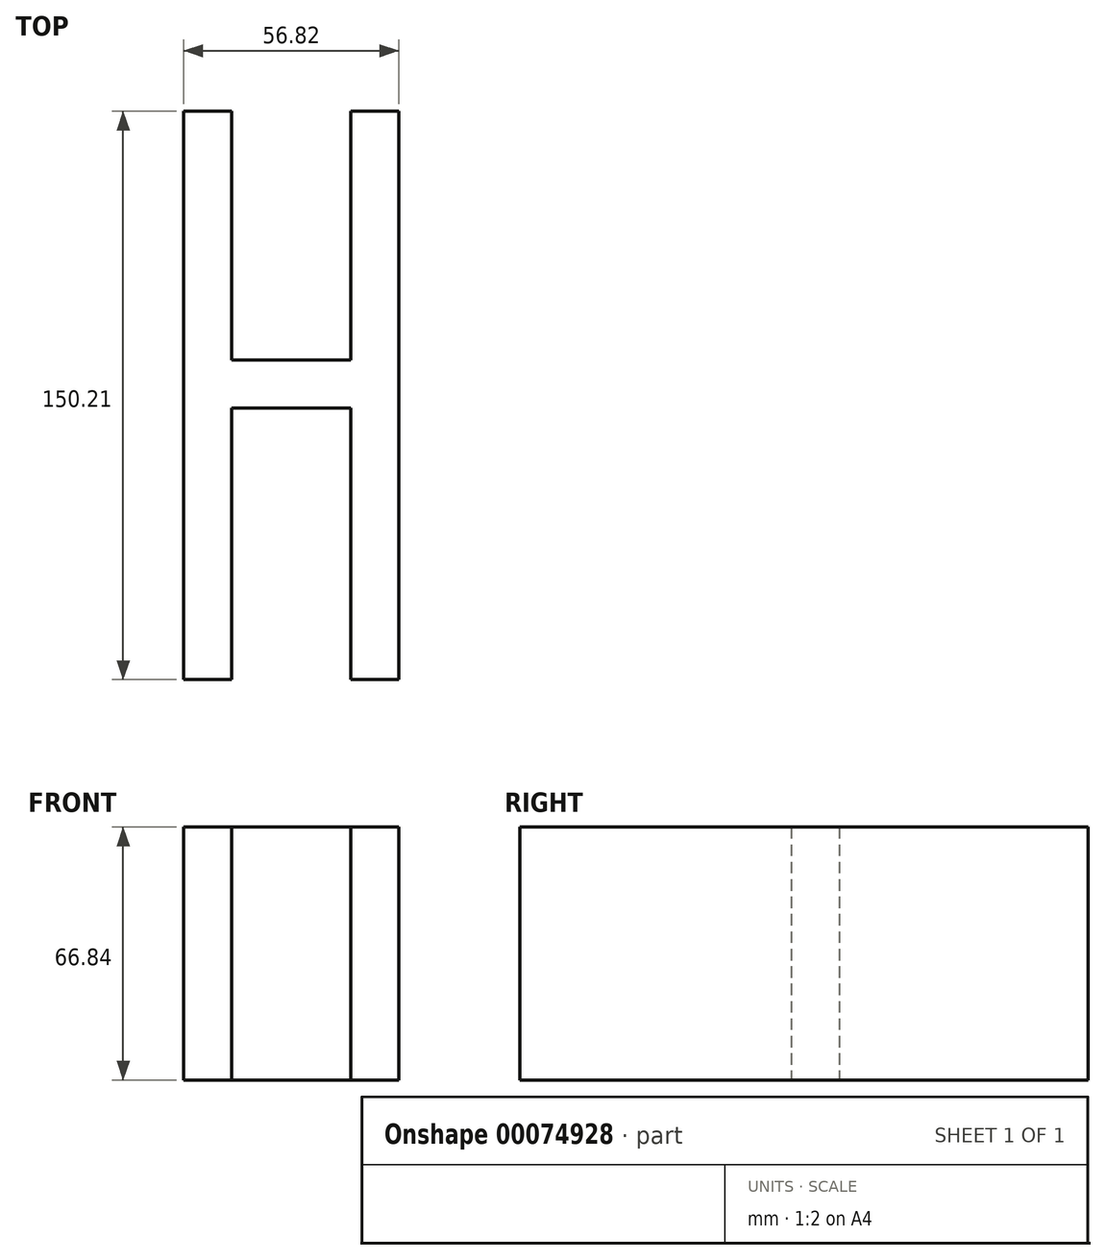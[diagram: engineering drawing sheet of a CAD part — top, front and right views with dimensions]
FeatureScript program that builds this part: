
annotation { "Feature Type Name" : "Feature", "Feature Type Description" : "" }
export const myFeature = defineFeature(function(context is Context, id is Id, definition is map)
    precondition{}
    {
        {
            var Q0;
            Q0=qCreatedBy(makeId("Top.planeOp"),FACE);
            var sketch = newSketch(context, id + "F0", { "sketchPlane" : qUnion([Q0])});
            skLineSegment(sketch, "E0.bottom", {"start": v(-111.8, 73) * mm, "end": v(-99.1, 73) * mm});
            skLineSegment(sketch, "E0.top", {"start": v(-111.8, -77.21) * mm, "end": v(-99.1, -77.21) * mm});
            skLineSegment(sketch, "E0.left", {"start": v(-111.8, 73) * mm, "end": v(-111.8, -77.21) * mm});
            skLineSegment(sketch, "E0.right", {"start": v(-99.1, 73) * mm, "end": v(-99.1, -77.21) * mm});
            skLineSegment(sketch, "E1.bottom", {"start": v(-67.67, 73) * mm, "end": v(-54.97, 73) * mm});
            skLineSegment(sketch, "E1.top", {"start": v(-67.67, -77.21) * mm, "end": v(-54.97, -77.21) * mm});
            skLineSegment(sketch, "E1.left", {"start": v(-67.67, 73) * mm, "end": v(-67.67, -77.21) * mm});
            skLineSegment(sketch, "E1.right", {"start": v(-54.97, 73) * mm, "end": v(-54.97, -77.21) * mm});
            skLineSegment(sketch, "E2.bottom", {"start": v(-99.1, 7.27) * mm, "end": v(-67.67, 7.27) * mm});
            skLineSegment(sketch, "E2.top", {"start": v(-99.1, -5.43) * mm, "end": v(-67.67, -5.43) * mm});
            skLineSegment(sketch, "E2.left", {"start": v(-99.1, 7.27) * mm, "end": v(-99.1, -5.43) * mm});
            skLineSegment(sketch, "E2.right", {"start": v(-67.67, 7.27) * mm, "end": v(-67.67, -5.43) * mm});
            skSolve(sketch);
        }
        {
            var Q0;
            {var subQ1=sQuery(id+"F0.wireOp",EDGE,"E0.bottom");Q0=makeQuery(id+"F0.imprint","IMPRINT",FACE,{"disambiguationData":[TD([[makeQuery(id+"F0.imprint","IMPRINT",EDGE,{"derivedFrom":subQ1}),-1.0]])]});}
            var Q1;
            Q1=makeQuery(id+"F0.imprint","IMPRINT",FACE,{"disambiguationData":[TD([[makeQuery(id+"F0.imprint","IMPRINT",EDGE,{"derivedFrom":sQuery(id+"F0.wireOp",EDGE,"E2.bottom")}),-1.0]])]});
            var Q2;
            {var subQ3=sQuery(id+"F0.wireOp",EDGE,"E1.bottom");Q2=makeQuery(id+"F0.imprint","IMPRINT",FACE,{"disambiguationData":[TD([[makeQuery(id+"F0.imprint","IMPRINT",EDGE,{"derivedFrom":subQ3}),-1.0]])]});}
            extrude(context, id + "F1", {"entities" : qUnion([Q0, Q1, Q2]), "depth" : 66.84 * mm});
        }
    });
